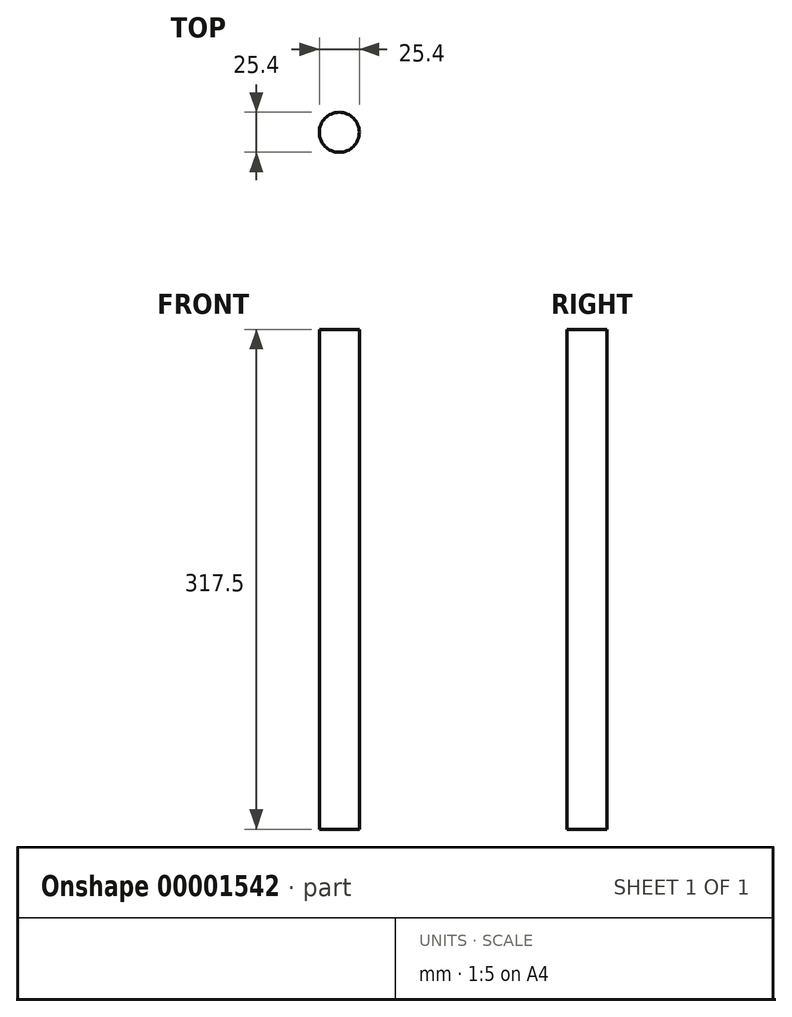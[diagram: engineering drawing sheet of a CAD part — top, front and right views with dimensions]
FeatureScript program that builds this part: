
annotation { "Feature Type Name" : "Feature", "Feature Type Description" : "" }
export const myFeature = defineFeature(function(context is Context, id is Id, definition is map)
    precondition{}
    {
        {
            var Q0;
            Q0=qCreatedBy(makeId("Top.planeOp"),FACE);
            var sketch = newSketch(context, id + "F0", { "sketchPlane" : qUnion([Q0])});
            skCircle(sketch, "E0", {"center": v(0, 0) * mm, "radius": 12.7 * mm});
            skSolve(sketch);
        }
        {
            var Q0;
            Q0=makeQuery(id+"F0.imprint","IMPRINT",FACE,{"disambiguationData":[TD([[makeQuery(id+"F0.imprint","IMPRINT",EDGE,{"derivedFrom":sQuery(id+"F0.wireOp",EDGE,"E0")}),1.0]])]});
            extrude(context, id + "F1", {"entities" : qUnion([Q0]), "depth" : 317.5 * mm});
        }
    });
